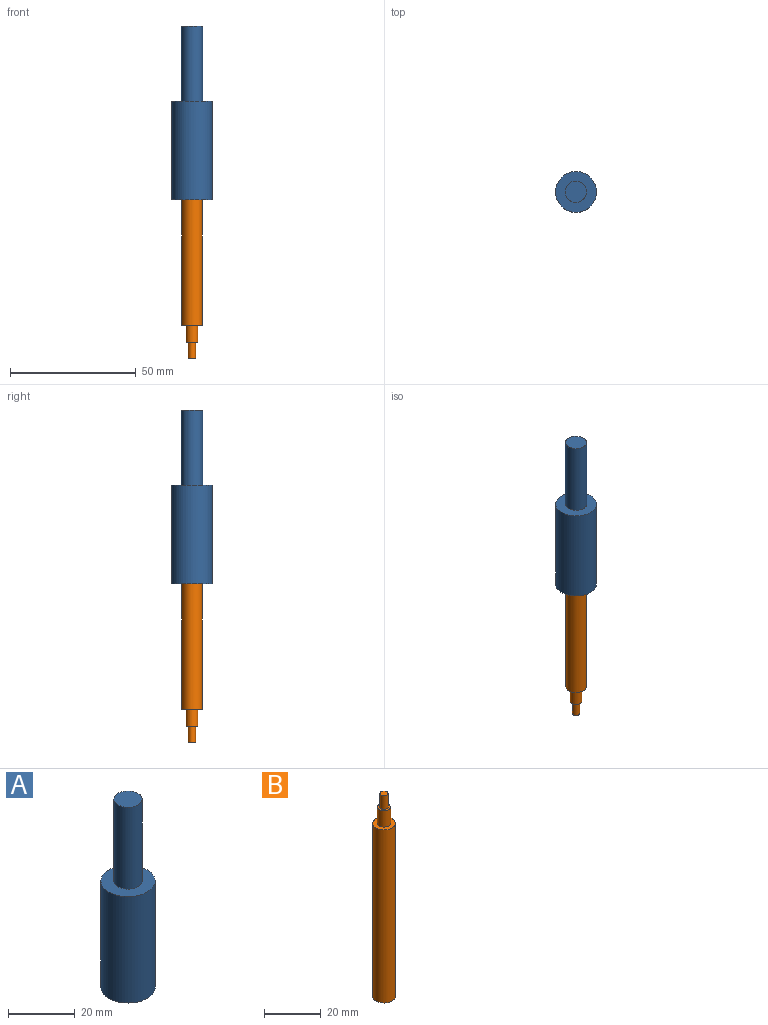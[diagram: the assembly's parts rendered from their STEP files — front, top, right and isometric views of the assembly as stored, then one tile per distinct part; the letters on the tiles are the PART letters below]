
ASSEMBLY  parts=2 mates=1
PART A: 7 faces, bbox 16.3x16.3x69 mm
  f0: cylinder r=8.12mm len=39mm, axis (0,0,-1), area 1991mm2, adj f1,f2
  f1: plane 16.25x16.25mm, normal (0,0,1), area 151.3mm2, adj f0,f3
  f2: plane 16.25x16.25mm, normal (0,0,-1), area 157.1mm2, adj f0,f5
  f3: cylinder r=4.22mm len=30mm, axis (0,0,-1), area 796.4mm2, adj f1,f4
  f4: plane 8.45x8.45mm, normal (0,0,1), area 56.1mm2, adj f3
  f5: cylinder r=4mm len=25mm, axis (0,0,-1), area 628.3mm2, adj f2,f6
  f6: plane 8x8mm, normal (0,0,-1), area 50.3mm2, adj f5
PART B: 7 faces, bbox 8x8x88 mm
  f0: cylinder r=4mm len=75mm, axis (0,0,-1), area 1885mm2, adj f1,f2
  f1: plane 8x8mm, normal (0,0,1), area 33.4mm2, adj f0,f3
  f2: plane 8x8mm, normal (0,0,-1), area 50.3mm2, adj f0
  f3: cylinder r=2.31mm len=7mm, axis (0,0,-1), area 101.8mm2, adj f1,f4
  f4: plane 4.63x4.63mm, normal (0,0,1), area 10.5mm2, adj f3,f5
  f5: cylinder r=1.42mm len=6mm, axis (0,0,-1), area 53.5mm2, adj f4,f6
  f6: plane 2.84x2.84mm, normal (0,0,1), area 6.3mm2, adj f5
PLACE A t=(1.14,23.04,-9.93)mm
PLACE B rot(axis=(1,0,0),180deg) t=(1.14,23.04,15.07)mm
MATE fastened B.f0 <-> A.f5  axis (0,0,1) through (1.14,23.04,15.07)mm
